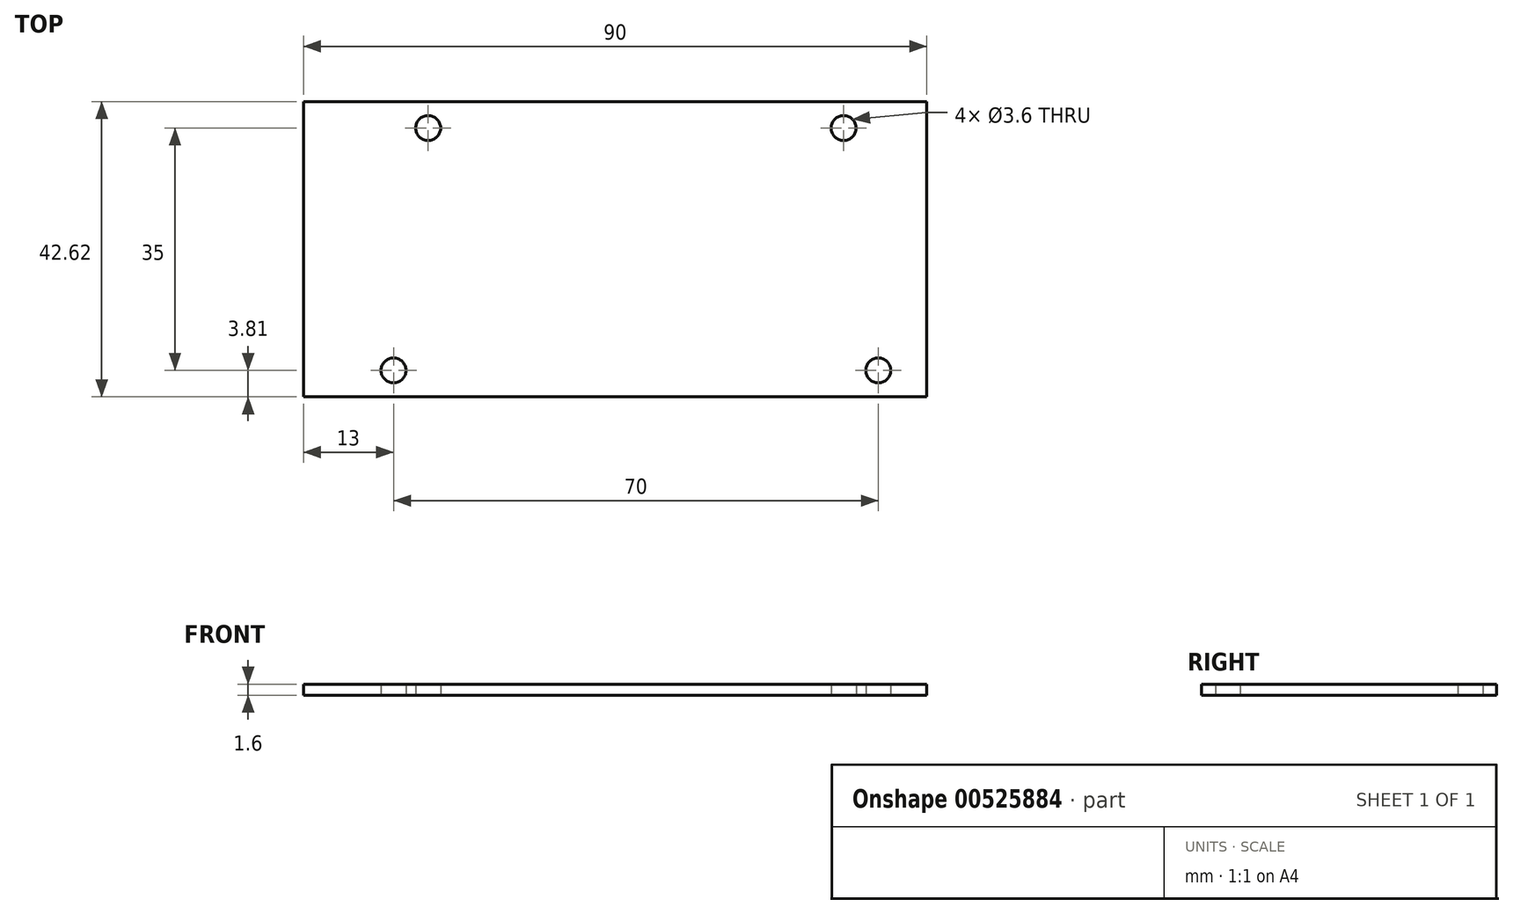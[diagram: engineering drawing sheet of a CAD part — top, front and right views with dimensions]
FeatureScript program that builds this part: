
annotation { "Feature Type Name" : "Feature", "Feature Type Description" : "" }
export const myFeature = defineFeature(function(context is Context, id is Id, definition is map)
    precondition{}
    {
        {
            var Q0;
            Q0=qCreatedBy(makeId("Top.planeOp"),FACE);
            var sketch = newSketch(context, id + "F0", { "sketchPlane" : qUnion([Q0])});
            skLineSegment(sketch, "E0.bottom", {"start": v(0, 0) * mm, "end": v(90, 0) * mm});
            skLineSegment(sketch, "E0.top", {"start": v(0, 42.62) * mm, "end": v(90, 42.62) * mm});
            skLineSegment(sketch, "E0.left", {"start": v(0, 0) * mm, "end": v(0, 42.62) * mm});
            skLineSegment(sketch, "E0.right", {"start": v(90, 0) * mm, "end": v(90, 42.62) * mm});
            skLineSegment(sketch, "E1", {"start": v(18, 38.8) * mm, "end": v(78, 38.8) * mm, "construction": true});
            skLineSegment(sketch, "E2", {"start": v(13, 3.81) * mm, "end": v(83, 3.81) * mm, "construction": true});
            skLineSegment(sketch, "E3", {"start": v(48, 38.8) * mm, "end": v(48, 3.81) * mm, "construction": true});
            skSolve(sketch);
        }
        {
            var Q0;
            Q0=makeQuery(id+"F0.imprint","IMPRINT",FACE,{"disambiguationData":[TD([[makeQuery(id+"F0.imprint","IMPRINT",EDGE,{"derivedFrom":sQuery(id+"F0.wireOp",EDGE,"E0.bottom")}),1.0]])]});
            extrude(context, id + "F1", {"entities" : qUnion([Q0]), "depth" : 1.6 * mm});
        }
        {
            var Q0;
            Q0=sQuery(id+"F0.wireOp",VERTEX,"E1.start");
            var Q1;
            Q1=sQuery(id+"F0.wireOp",VERTEX,"E2.start");
            var Q2;
            Q2=sQuery(id+"F0.wireOp",VERTEX,"E1.end");
            var Q3;
            Q3=sQuery(id+"F0.wireOp",VERTEX,"E2.end");
            var Q4;
            Q4=makeQuery(id+"F1.opExtrude","SWEPT_BODY",BODY,{"disambiguationData":[OSD([sQuery(id+"F0.wireOp",EDGE,"E0.bottom"),sQuery(id+"F0.wireOp",EDGE,"E0.top"),sQuery(id+"F0.wireOp",EDGE,"E0.left"),sQuery(id+"F0.wireOp",EDGE,"E0.right")])]});
            hole(context, id + "F2", {"style" : HoleStyle.SIMPLE, "endStyle" : HoleEndStyle.THROUGH, "oppositeDirection" : true, "holeDiameter" : 3.6 * mm, "isTappedThrough" : true, "tappedDepth" : 12 * mm, "tapClearance" : 3, "locations" : qUnion([Q0, Q1, Q2, Q3]), "scope" : qUnion([Q4])});
        }
    });
